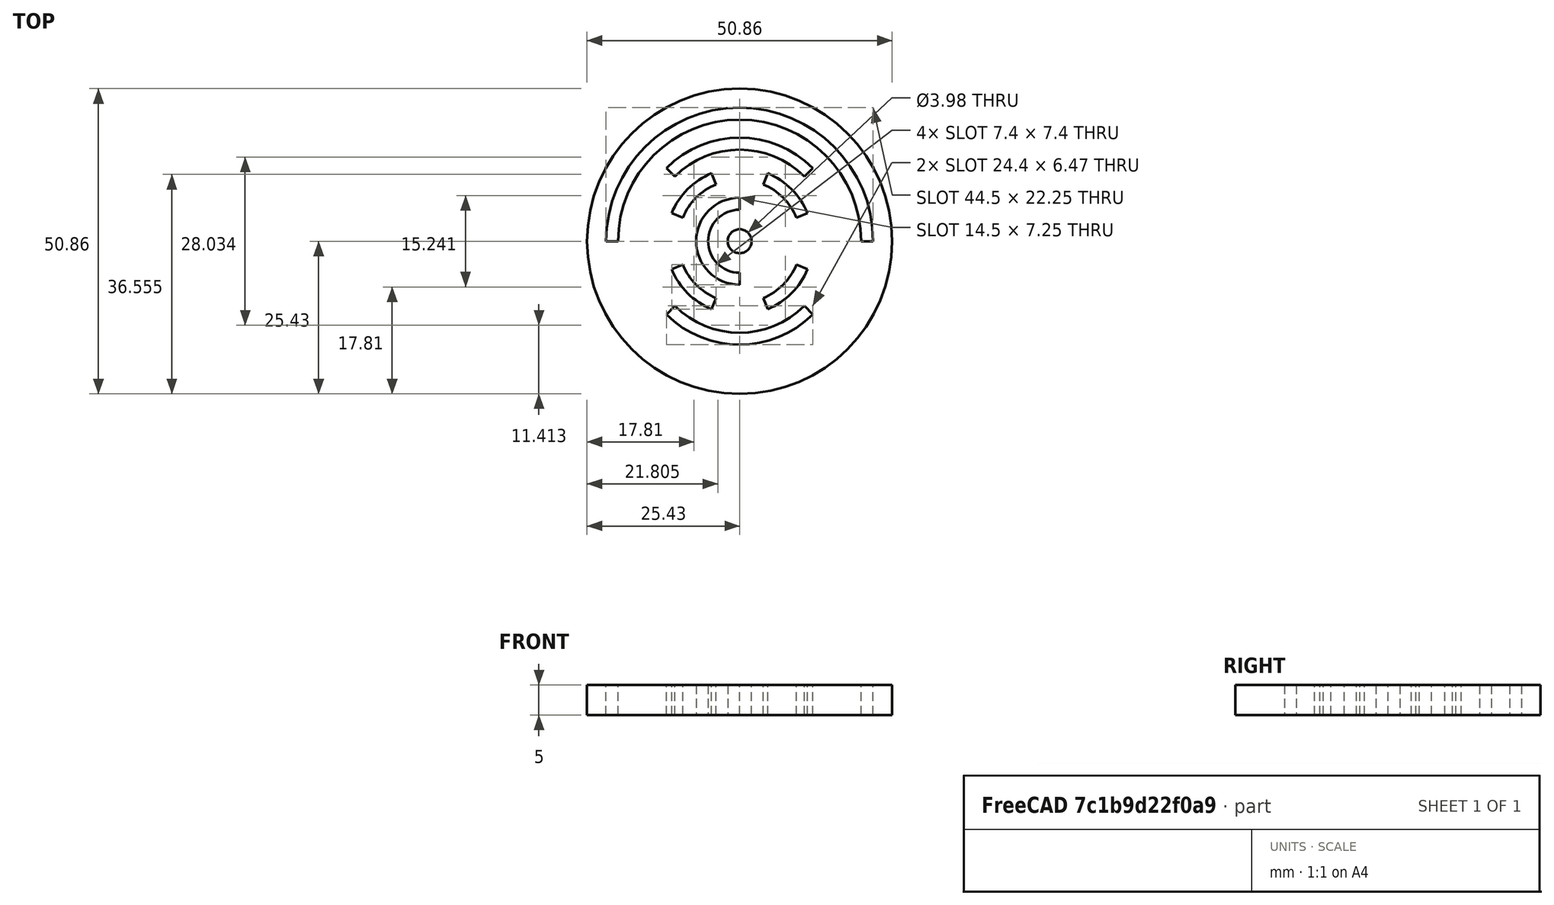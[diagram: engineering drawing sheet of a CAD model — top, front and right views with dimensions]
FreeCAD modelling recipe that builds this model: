
FCSTD DOCUMENT  (FreeCAD 0.18R16131 (Git))
Label: disco_4bit
License: All rights reserved
LicenseURL: http://en.wikipedia.org/wiki/All_rights_reserved
objects: Sketcher::SketchObject×1, PartDesign::Pad×1, PartDesign::Body×1
note: 4 computed .brp shape members not serialized (recipe doc carries the construction recipe); baked Part::Feature solids carry a one-line shape summary decoded from their .brp

FEATURE [Sketcher::SketchObject] Sketch
  MapMode = 5
  Support = -> [XY_Plane]
  sketch-geometry (61):
    g0: Circle CenterX=0 CenterY=0 CenterZ=0 NormalX=0 NormalY=0 NormalZ=1 AngleXU=0 Radius=25.4264
    g1: Circle CenterX=0 CenterY=0 CenterZ=0 NormalX=0 NormalY=0 NormalZ=1 AngleXU=0 Radius=1.99134
    g2: LineSegment StartX=-22.2504 StartY=2.7e-15 StartZ=0 EndX=-20.2504 EndY=0 EndZ=0
    g3: LineSegment StartX=20.2504 StartY=0 StartZ=0 EndX=22.2504 EndY=0 EndZ=0
    g4: LineSegment [constr] StartX=0 StartY=0 StartZ=0 EndX=25.4833 EndY=25.4833 EndZ=0
    g5: LineSegment [constr] StartX=0 StartY=0 StartZ=0 EndX=-25.6228 EndY=25.6228 EndZ=0
    g6: ArcOfCircle CenterX=0 CenterY=0 CenterZ=0 NormalX=0 NormalY=0 NormalZ=1 AngleXU=0 Radius=17.2504 StartAngle=0.785398 EndAngle=2.35619
    g7: ArcOfCircle CenterX=0 CenterY=0 CenterZ=0 NormalX=0 NormalY=0 NormalZ=1 AngleXU=0 Radius=15.2504 StartAngle=0.785398 EndAngle=2.35619
    g8: LineSegment StartX=-12.1979 StartY=12.1979 StartZ=0 EndX=-10.7837 EndY=10.7837 EndZ=0
    g9: LineSegment StartX=10.7837 StartY=10.7837 StartZ=0 EndX=12.1979 EndY=12.1979 EndZ=0
    g10: LineSegment StartX=10.7837 StartY=-10.7837 StartZ=0 EndX=12.1979 EndY=-12.1979 EndZ=0
    g11: ArcOfCircle CenterX=0 CenterY=0 CenterZ=0 NormalX=0 NormalY=0 NormalZ=1 AngleXU=0 Radius=15.2504 StartAngle=3.92699 EndAngle=5.49779
    g12: ArcOfCircle CenterX=0 CenterY=0 CenterZ=0 NormalX=0 NormalY=0 NormalZ=1 AngleXU=0 Radius=17.2504 StartAngle=3.92699 EndAngle=5.49779
    g13: LineSegment StartX=-12.1979 StartY=-12.1979 StartZ=0 EndX=-10.7837 EndY=-10.7837 EndZ=0
    g14: LineSegment [constr] StartX=0 StartY=0 StartZ=0 EndX=12.4775 EndY=30.1234 EndZ=0
    g15: LineSegment [constr] StartX=0 StartY=0 StartZ=0 EndX=-12.5373 EndY=30.2678 EndZ=0
    g16: LineSegment [constr] StartX=0 StartY=0 StartZ=0 EndX=30.1032 EndY=12.4692 EndZ=0
    g17: LineSegment [constr] StartX=0 StartY=0 StartZ=0 EndX=-30.0731 EndY=12.4567 EndZ=0
    g18: ArcOfCircle CenterX=0 CenterY=0 CenterZ=0 NormalX=0 NormalY=0 NormalZ=1 AngleXU=0 Radius=12.2504 StartAngle=1.9635 EndAngle=2.74889
    g19: ArcOfCircle CenterX=0 CenterY=0 CenterZ=0 NormalX=0 NormalY=0 NormalZ=1 AngleXU=0 Radius=10.2504 StartAngle=1.9635 EndAngle=2.74889
    g20: LineSegment StartX=-4.68802 StartY=11.3179 StartZ=0 EndX=-3.92266 EndY=9.47013 EndZ=0
    g21: LineSegment StartX=-11.3179 StartY=4.68802 StartZ=0 EndX=-9.47013 EndY=3.92266 EndZ=0
    g22: ArcOfCircle CenterX=0 CenterY=0 CenterZ=0 NormalX=0 NormalY=0 NormalZ=1 AngleXU=0 Radius=12.2504 StartAngle=0.392699 EndAngle=1.1781
    g23: ArcOfCircle CenterX=0 CenterY=0 CenterZ=0 NormalX=0 NormalY=0 NormalZ=1 AngleXU=0 Radius=10.2504 StartAngle=0.392699 EndAngle=1.1781
    g24: LineSegment StartX=4.68802 StartY=11.3179 StartZ=0 EndX=3.92266 EndY=9.47013 EndZ=0
    g25: LineSegment StartX=11.3179 StartY=4.68802 StartZ=0 EndX=9.47013 EndY=3.92266 EndZ=0
    g26: ArcOfCircle CenterX=0 CenterY=0 CenterZ=0 NormalX=0 NormalY=0 NormalZ=1 AngleXU=0 Radius=12.2504 StartAngle=3.53429 EndAngle=4.31969
    g27: ArcOfCircle CenterX=0 CenterY=0 CenterZ=0 NormalX=0 NormalY=0 NormalZ=1 AngleXU=0 Radius=10.2504 StartAngle=3.53429 EndAngle=4.31969
    g28: LineSegment StartX=-4.68802 StartY=-11.3179 StartZ=0 EndX=-3.92266 EndY=-9.47013 EndZ=0
    g29: LineSegment StartX=-11.3179 StartY=-4.68802 StartZ=0 EndX=-9.47013 EndY=-3.92266 EndZ=0
    g30: ArcOfCircle CenterX=0 CenterY=0 CenterZ=0 NormalX=0 NormalY=0 NormalZ=1 AngleXU=0 Radius=10.2504 StartAngle=5.10509 EndAngle=5.89049
    g31: ArcOfCircle CenterX=0 CenterY=0 CenterZ=0 NormalX=0 NormalY=0 NormalZ=1 AngleXU=0 Radius=12.2504 StartAngle=5.10509 EndAngle=5.89049
    g32: LineSegment StartX=4.68802 StartY=-11.3179 StartZ=0 EndX=3.92266 EndY=-9.47013 EndZ=0
    g33: LineSegment StartX=11.3179 StartY=-4.68802 StartZ=0 EndX=9.47013 EndY=-3.92266 EndZ=0
    g34: ArcOfCircle CenterX=0 CenterY=0 CenterZ=0 NormalX=0 NormalY=0 NormalZ=1 AngleXU=0 Radius=7.25039 StartAngle=1.5708 EndAngle=4.71239
    g35: ArcOfCircle CenterX=0 CenterY=0 CenterZ=0 NormalX=0 NormalY=0 NormalZ=1 AngleXU=0 Radius=5.25039 StartAngle=1.5708 EndAngle=4.71239
    g36: LineSegment StartX=0 StartY=7.25039 StartZ=0 EndX=3e-16 EndY=5.25039 EndZ=0
    g37: LineSegment StartX=-1e-15 StartY=-5.25039 StartZ=0 EndX=0 EndY=-7.25039 EndZ=0
    g38: LineSegment [constr] StartX=0 StartY=0 StartZ=0 EndX=-30.1019 EndY=-12.4686 EndZ=0
    g39: LineSegment [constr] StartX=0 StartY=0 StartZ=0 EndX=-25.3748 EndY=-25.3748 EndZ=0
    g40: LineSegment [constr] StartX=0 StartY=0 StartZ=0 EndX=-12.4863 EndY=-30.1446 EndZ=0
    g41: LineSegment [constr] StartX=0 StartY=0 StartZ=0 EndX=25.2108 EndY=-25.2108 EndZ=0
    g42: LineSegment [constr] StartX=0 StartY=0 StartZ=0 EndX=30.116 EndY=-12.4745 EndZ=0
    g43: LineSegment [constr] StartX=0 StartY=0 StartZ=0 EndX=12.4691 EndY=-30.1031 EndZ=0
    g44: Circle [constr] CenterX=0 CenterY=0 CenterZ=0 NormalX=0 NormalY=0 NormalZ=1 AngleXU=0 Radius=5.25039
    g45: Circle [constr] CenterX=0 CenterY=0 CenterZ=0 NormalX=0 NormalY=0 NormalZ=1 AngleXU=0 Radius=7.25039
    g46: Circle [constr] CenterX=4e-16 CenterY=-8e-16 CenterZ=0 NormalX=0 NormalY=0 NormalZ=1 AngleXU=0 Radius=10.2504
    g47: Circle [constr] CenterX=0 CenterY=0 CenterZ=0 NormalX=0 NormalY=0 NormalZ=1 AngleXU=0 Radius=12.2504
    g48: Circle [constr] CenterX=0 CenterY=0 CenterZ=0 NormalX=0 NormalY=0 NormalZ=1 AngleXU=0 Radius=17.2504
    g49: Circle [constr] CenterX=0 CenterY=0 CenterZ=0 NormalX=0 NormalY=0 NormalZ=1 AngleXU=0 Radius=20.2504
    g50: Circle [constr] CenterX=0 CenterY=0 CenterZ=0 NormalX=0 NormalY=0 NormalZ=1 AngleXU=0 Radius=22.2504
    g51: LineSegment [constr] StartX=0 StartY=0 StartZ=0 EndX=35.7654 EndY=0 EndZ=0
    g52: LineSegment [constr] StartX=0 StartY=0 StartZ=0 EndX=-35.6552 EndY=0 EndZ=0
    g53: LineSegment [constr] StartX=0 StartY=0 StartZ=0 EndX=0 EndY=35.6156 EndZ=0
    g54: LineSegment [constr] StartX=0 StartY=0 StartZ=0 EndX=-0.0176703 EndY=-35.7721 EndZ=0
    g55: LineSegment [constr] StartX=5.25039 StartY=0 StartZ=0 EndX=7.25039 EndY=0 EndZ=0
    g56: LineSegment [constr] StartX=10.2504 StartY=0 StartZ=0 EndX=12.2504 EndY=0 EndZ=0
    g57: ArcOfCircle CenterX=0 CenterY=0 CenterZ=0 NormalX=0 NormalY=0 NormalZ=1 AngleXU=0 Radius=20.2504 StartAngle=0 EndAngle=3.14159
    g58: ArcOfCircle CenterX=0 CenterY=0 CenterZ=0 NormalX=0 NormalY=0 NormalZ=1 AngleXU=0 Radius=22.2504 StartAngle=0 EndAngle=3.14159
    g59: Circle [constr] CenterX=0 CenterY=0 CenterZ=0 NormalX=0 NormalY=0 NormalZ=1 AngleXU=0 Radius=15.2504
    g60: LineSegment [constr] StartX=15.2504 StartY=0 StartZ=0 EndX=17.2504 EndY=0 EndZ=0
  constraints (157):
    c: PointOnObject(g3,g-1)
    c: PointOnObject(g2,g-1)
    c: PointOnObject(g2,g-1)
    c: PointOnObject(g6,g5)
    c: PointOnObject(g6,g4)
    c: PointOnObject(g7,g5)
    c: Coincident(g8,g6)
    c: Coincident(g8,g7)
    c: Coincident(g9,g7)
    c: Coincident(g9,g6)
    c: Coincident(g13,g12)
    c: Coincident(g13,g11)
    c: Coincident(g10,g11)
    c: Coincident(g10,g12)
    c: Angle(g14,g-2) = 0.392699
    c: PointOnObject(g18,g17)
    c: PointOnObject(g18,g15)
    c: PointOnObject(g19,g17)
    c: PointOnObject(g19,g15)
    c: Coincident(g20,g18)
    c: Coincident(g20,g19)
    c: Coincident(g21,g18)
    c: Coincident(g21,g19)
    c: Coincident(g24,g22)
    c: Coincident(g24,g23)
    c: Coincident(g25,g22)
    c: Coincident(g25,g23)
    c: Coincident(g28,g26)
    c: Coincident(g28,g27)
    c: Coincident(g29,g26)
    c: Coincident(g29,g27)
    c: Coincident(g32,g31)
    c: Coincident(g32,g30)
    c: Coincident(g33,g31)
    c: Coincident(g33,g30)
    c: PointOnObject(g34,g-2)
    c: PointOnObject(g35,g-2)
    c: PointOnObject(g35,g-2)
    c: Coincident(g36,g34)
    c: Coincident(g36,g35)
    c: Coincident(g37,g35)
    c: Coincident(g37,g34)
    c: PointOnObject(g35,g44)
    c: PointOnObject(g34,g45)
    c: PointOnObject(g6,g48)
    c: PointOnObject(g18,g47)
    c: PointOnObject(g55,g44)
    c: PointOnObject(g55,g45)
    c: Horizontal(g55)
    c: PointOnObject(g56,g46)
    c: PointOnObject(g56,g47)
    c: Horizontal(g56)
    c: Coincident(g15,g-1)
    c: Coincident(g17,g-1)
    c: Coincident(g5,g-1)
    c: Coincident(g38,g-1)
    c: Coincident(g40,g-1)
    c: Coincident(g50,g-1)
    c: Coincident(g-1,g52)
    c: Coincident(g19,g-1)
    c: Coincident(g47,g19)
    c: Coincident(g30,g19)
    c: Coincident(g31,g19)
    c: Coincident(g34,g19)
    c: Coincident(g35,g19)
    c: Coincident(g45,g19)
    c: Coincident(g49,g19)
    c: Coincident(g1,g19)
    c: Coincident(g54,g1)
    c: Coincident(g0,g1)
    c: Coincident(g44,g0)
    c: Coincident(g22,g0)
    c: Coincident(g18,g0)
    c: Coincident(g12,g0)
    c: Coincident(g23,g0)
    c: Coincident(g7,g0)
    c: Coincident(g6,g0)
    c: Coincident(g26,g0)
    c: Coincident(g27,g0)
    c: Coincident(g11,g0)
    c: Coincident(g48,g0)
    c: Coincident(g4,g0)
    c: PointOnObject(g34,g53)
    c: PointOnObject(g35,g53)
    c: PointOnObject(g22,g47)
    c: PointOnObject(g22,g16)
    c: PointOnObject(g23,g46)
    c: PointOnObject(g23,g16)
    c: PointOnObject(g23,g14)
    c: PointOnObject(g22,g14)
    c: PointOnObject(g23,g46)
    c: PointOnObject(g19,g46)
    c: PointOnObject(g19,g46)
    c: PointOnObject(g30,g46)
    c: PointOnObject(g31,g47)
    c: PointOnObject(g31,g43)
    c: PointOnObject(g30,g43)
    c: PointOnObject(g27,g40)
    c: PointOnObject(g27,g46)
    c: PointOnObject(g26,g47)
    c: PointOnObject(g26,g40)
    c: PointOnObject(g26,g38)
    c: PointOnObject(g27,g38)
    c: Coincident(g0,g53)
    c: Coincident(g16,g0)
    c: Coincident(g14,g0)
    c: Coincident(g43,g0)
    c: PointOnObject(g3,g51)
    c: PointOnObject(g3,g50)
    c: PointOnObject(g3,g49)
    c: Coincident(g0,g51)
    c: PointOnObject(g2,g52)
    c: PointOnObject(g3,g51)
    c: Coincident(g57,g0)
    c: Coincident(g57,g2)
    c: Coincident(g57,g3)
    c: Coincident(g58,g0)
    c: Coincident(g58,g2)
    c: Coincident(g58,g3)
    c: Coincident(g59,g0)
    c: PointOnObject(g7,g59)
    c: PointOnObject(g11,g59)
    c: PointOnObject(g12,g48)
    c: PointOnObject(g10,g41)
    c: PointOnObject(g10,g41)
    c: PointOnObject(g7,g4)
    c: Angle(g4,g14) = 0.392699
    c: Angle(g16,g4) = 0.392699
    c: Angle(g42,g16) = 0.785398
    c: Angle(g41,g42) = 0.392699
    c: Angle(g43,g41) = 0.392699
    c: Angle(g40,g43) = 0.785398
    c: Angle(g39,g40) = 0.392699
    c: PointOnObject(g11,g39)
    c: PointOnObject(g12,g39)
    c: Coincident(g39,g0)
    c: Coincident(g41,g0)
    c: Angle(g38,g39) = 0.392699
    c: Angle(g17,g38) = 0.785398
    c: Angle(g5,g17) = 0.392699
    c: Angle(g15,g5) = 0.392699
    c: PointOnObject(g30,g42)
    c: PointOnObject(g31,g42)
    c: PointOnObject(g60,g59)
    c: PointOnObject(g60,g51)
    c: PointOnObject(g60,g48)
    c: PointOnObject(g60,g51)
    c: DistanceX(g60,g60) = 2
    c: DistanceX(g3,g3) = 2
    c: PointOnObject(g56,g51)
    c: DistanceX(g56,g56) = 2
    c: PointOnObject(g55,g51)
    c: DistanceX(g55,g55) = 2
    c: DistanceX(g55,g56) = 3
    c: DistanceX(g56,g60) = 3
    c: DistanceX(g60,g3) = 3
    c: Coincident(g42,g0)
FEATURE [PartDesign::Pad] Pad
  Length = 5
  Length2 = 100
  Profile = -> Sketch
  Type = 0
FEATURE [PartDesign::Body] Body
  Group = -> [Sketch,Pad]
  Origin = -> Origin
  Tip = -> Pad
